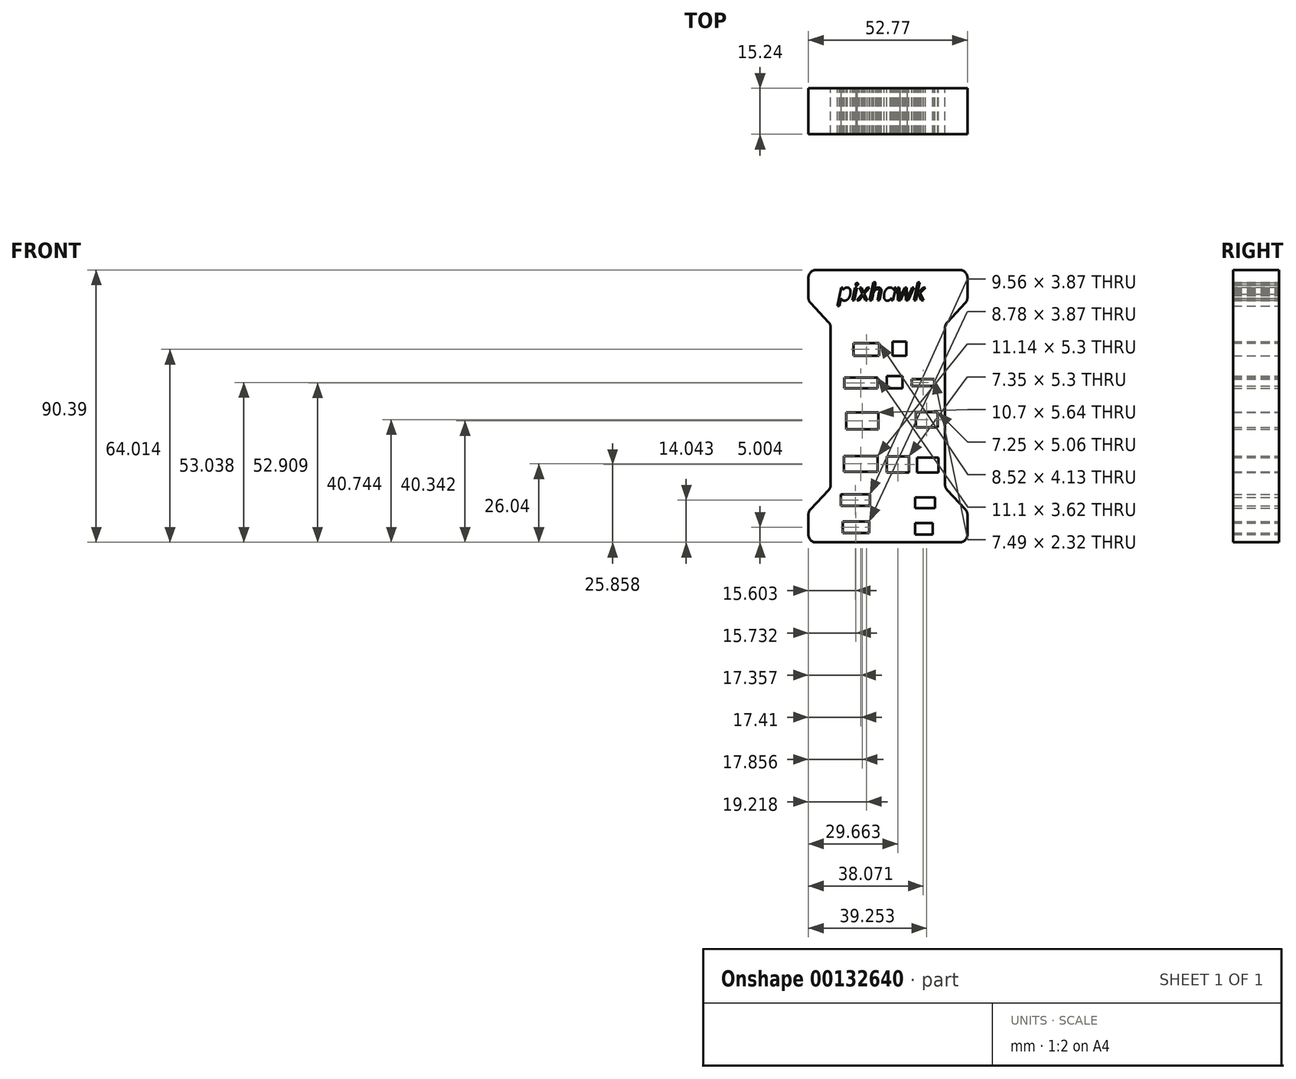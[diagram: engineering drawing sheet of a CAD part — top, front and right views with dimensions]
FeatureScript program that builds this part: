
annotation { "Feature Type Name" : "Feature", "Feature Type Description" : "" }
export const myFeature = defineFeature(function(context is Context, id is Id, definition is map)
    precondition{}
    {
        {
            var Q0;
            Q0=qCreatedBy(makeId("Front.planeOp"),FACE);
            var sketch = newSketch(context, id + "F0", { "sketchPlane" : qUnion([Q0])});
            skText(sketch, "E0", { "text": "pixhawk", "fontName": "OpenSans-Italic.ttf"});
            skLineSegment(sketch, "E1.bottom", {"start": v(-12.44, 30.78) * mm, "end": v(-3.92, 30.78) * mm});
            skLineSegment(sketch, "E1.top", {"start": v(-12.44, 26.65) * mm, "end": v(-3.92, 26.65) * mm});
            skLineSegment(sketch, "E1.left", {"start": v(-12.44, 30.78) * mm, "end": v(-12.44, 26.65) * mm});
            skLineSegment(sketch, "E1.right", {"start": v(-3.92, 30.78) * mm, "end": v(-3.92, 26.65) * mm});
            skLineSegment(sketch, "E2.bottom", {"start": v(0.47, 31.3) * mm, "end": v(5.12, 31.3) * mm});
            skLineSegment(sketch, "E2.top", {"start": v(0.47, 26.65) * mm, "end": v(5.12, 26.65) * mm});
            skLineSegment(sketch, "E2.left", {"start": v(0.47, 31.3) * mm, "end": v(0.47, 26.65) * mm});
            skLineSegment(sketch, "E2.right", {"start": v(5.12, 31.3) * mm, "end": v(5.12, 26.65) * mm});
            skLineSegment(sketch, "E3.bottom", {"start": v(-15.54, 19.42) * mm, "end": v(-4.44, 19.42) * mm});
            skLineSegment(sketch, "E3.top", {"start": v(-15.54, 15.8) * mm, "end": v(-4.44, 15.8) * mm});
            skLineSegment(sketch, "E3.left", {"start": v(-15.54, 19.42) * mm, "end": v(-15.54, 15.8) * mm});
            skLineSegment(sketch, "E3.right", {"start": v(-4.44, 19.42) * mm, "end": v(-4.44, 15.8) * mm});
            skLineSegment(sketch, "E4.bottom", {"start": v(-1.41, 19.93) * mm, "end": v(3.83, 19.93) * mm});
            skLineSegment(sketch, "E4.top", {"start": v(-1.41, 15.8) * mm, "end": v(3.83, 15.8) * mm});
            skLineSegment(sketch, "E4.left", {"start": v(-1.41, 19.93) * mm, "end": v(-1.41, 15.8) * mm});
            skLineSegment(sketch, "E4.right", {"start": v(3.83, 19.93) * mm, "end": v(3.83, 15.8) * mm});
            skLineSegment(sketch, "E5.bottom", {"start": v(6.93, 18.9) * mm, "end": v(14.42, 18.9) * mm});
            skLineSegment(sketch, "E5.top", {"start": v(6.93, 16.58) * mm, "end": v(14.42, 16.58) * mm});
            skLineSegment(sketch, "E5.left", {"start": v(6.93, 18.9) * mm, "end": v(6.93, 16.58) * mm});
            skLineSegment(sketch, "E5.right", {"start": v(14.42, 18.9) * mm, "end": v(14.42, 16.58) * mm});
            skLineSegment(sketch, "E6.bottom", {"start": v(-16.57, -19.32) * mm, "end": v(-7.02, -19.32) * mm});
            skLineSegment(sketch, "E6.top", {"start": v(-16.57, -23.2) * mm, "end": v(-7.02, -23.2) * mm});
            skLineSegment(sketch, "E6.left", {"start": v(-16.57, -19.32) * mm, "end": v(-16.57, -23.2) * mm});
            skLineSegment(sketch, "E6.right", {"start": v(-7.02, -19.32) * mm, "end": v(-7.02, -23.2) * mm});
            skLineSegment(sketch, "E7.bottom", {"start": v(-16.06, -28.36) * mm, "end": v(-7.28, -28.36) * mm});
            skLineSegment(sketch, "E7.top", {"start": v(-16.06, -32.23) * mm, "end": v(-7.28, -32.23) * mm});
            skLineSegment(sketch, "E7.left", {"start": v(-16.06, -28.36) * mm, "end": v(-16.06, -32.23) * mm});
            skLineSegment(sketch, "E7.right", {"start": v(-7.28, -28.36) * mm, "end": v(-7.28, -32.23) * mm});
            skLineSegment(sketch, "E8.bottom", {"start": v(7.96, -20.35) * mm, "end": v(14.67, -20.35) * mm});
            skLineSegment(sketch, "E8.top", {"start": v(7.96, -23.97) * mm, "end": v(14.67, -23.97) * mm});
            skLineSegment(sketch, "E8.left", {"start": v(7.96, -20.35) * mm, "end": v(7.96, -23.97) * mm});
            skLineSegment(sketch, "E8.right", {"start": v(14.67, -20.35) * mm, "end": v(14.67, -23.97) * mm});
            skLineSegment(sketch, "E9.bottom", {"start": v(7.96, -28.88) * mm, "end": v(13.9, -28.88) * mm});
            skLineSegment(sketch, "E9.top", {"start": v(7.96, -32.75) * mm, "end": v(13.9, -32.75) * mm});
            skLineSegment(sketch, "E9.left", {"start": v(7.96, -28.88) * mm, "end": v(7.96, -32.75) * mm});
            skLineSegment(sketch, "E9.right", {"start": v(13.9, -28.88) * mm, "end": v(13.9, -32.75) * mm});
            skLineSegment(sketch, "E10.bottom", {"start": v(-15.61, -6.61) * mm, "end": v(-4.47, -6.61) * mm});
            skLineSegment(sketch, "E10.top", {"start": v(-15.61, -11.9) * mm, "end": v(-4.47, -11.9) * mm});
            skLineSegment(sketch, "E10.left", {"start": v(-15.61, -6.61) * mm, "end": v(-15.61, -11.9) * mm});
            skLineSegment(sketch, "E10.right", {"start": v(-4.47, -6.61) * mm, "end": v(-4.47, -11.9) * mm});
            skLineSegment(sketch, "E11.bottom", {"start": v(-1.41, -6.8) * mm, "end": v(5.94, -6.8) * mm});
            skLineSegment(sketch, "E11.top", {"start": v(-1.41, -12.1) * mm, "end": v(5.94, -12.1) * mm});
            skLineSegment(sketch, "E11.left", {"start": v(-1.41, -6.8) * mm, "end": v(-1.41, -12.1) * mm});
            skLineSegment(sketch, "E11.right", {"start": v(5.94, -6.8) * mm, "end": v(5.94, -12.1) * mm});
            skLineSegment(sketch, "E12.bottom", {"start": v(8.68, -7.16) * mm, "end": v(15.8, -7.16) * mm});
            skLineSegment(sketch, "E12.top", {"start": v(8.68, -12.1) * mm, "end": v(15.8, -12.1) * mm});
            skLineSegment(sketch, "E12.left", {"start": v(8.68, -7.16) * mm, "end": v(8.68, -12.1) * mm});
            skLineSegment(sketch, "E12.right", {"start": v(15.8, -7.16) * mm, "end": v(15.8, -12.1) * mm});
            skLineSegment(sketch, "E13.bottom", {"start": v(-14.9, 7.86) * mm, "end": v(-4.2, 7.86) * mm});
            skLineSegment(sketch, "E13.top", {"start": v(-14.9, 2.22) * mm, "end": v(-4.2, 2.22) * mm});
            skLineSegment(sketch, "E13.left", {"start": v(-14.9, 7.86) * mm, "end": v(-14.9, 2.22) * mm});
            skLineSegment(sketch, "E13.right", {"start": v(-4.2, 7.86) * mm, "end": v(-4.2, 2.22) * mm});
            skLineSegment(sketch, "E14.bottom", {"start": v(8.23, 7.98) * mm, "end": v(15.48, 7.98) * mm});
            skLineSegment(sketch, "E14.top", {"start": v(8.23, 2.91) * mm, "end": v(15.48, 2.91) * mm});
            skLineSegment(sketch, "E14.left", {"start": v(8.23, 7.98) * mm, "end": v(8.23, 2.91) * mm});
            skLineSegment(sketch, "E14.right", {"start": v(15.48, 7.98) * mm, "end": v(15.48, 2.91) * mm});
            skLineSegment(sketch, "E15.top", {"start": v(24.97, 9.52) * mm, "end": v(-27.8, 9.52) * mm});
            skLineSegment(sketch, "E16.bottom", {"start": v(25.37, -35.3) * mm, "end": v(-27.4, -35.3) * mm});
            skLineSegment(sketch, "E16.top", {"start": v(25.37, 55.1) * mm, "end": v(-27.4, 55.1) * mm});
            skLineSegment(sketch, "E16.left", {"start": v(25.37, -35.3) * mm, "end": v(25.37, -25.07) * mm});
            skLineSegment(sketch, "E16.right", {"start": v(-27.4, -35.3) * mm, "end": v(-27.4, -25.07) * mm});
            skPoint(sketch, "E16.middle", {"position": v(-1.02, 9.9) * mm});
            skLineSegment(sketch, "E17.left", {"start": v(17.97, -17.2) * mm, "end": v(17.97, 36.99) * mm});
            skLineSegment(sketch, "E17.right", {"start": v(-20, -17.2) * mm, "end": v(-20, 36.99) * mm});
            skLineSegment(sketch, "E18", {"start": v(25.37, -25.07) * mm, "end": v(17.97, -17.2) * mm});
            skLineSegment(sketch, "E19.MirrorCS", {"start": v(-27.4, -25.07) * mm, "end": v(-20, -17.2) * mm});
            skLineSegment(sketch, "E20.MirrorCS", {"start": v(25.37, 44.87) * mm, "end": v(17.97, 36.99) * mm});
            skLineSegment(sketch, "E21.MirrorCS", {"start": v(-27.4, 44.87) * mm, "end": v(-20, 36.99) * mm});
            skLineSegment(sketch, "E22.trimOffspring", {"start": v(25.37, 44.87) * mm, "end": v(25.37, 55.1) * mm});
            skPoint(sketch, "E17.bottom.start.orphan", {"position": v(17.97, -22.79) * mm});
            skPoint(sketch, "E23.orphan", {"position": v(-20, -22.79) * mm});
            skPoint(sketch, "E17.top.start.orphan", {"position": v(17.97, 42.58) * mm});
            skPoint(sketch, "E24.orphan", {"position": v(-20, 42.58) * mm});
            skLineSegment(sketch, "E25.trimOffspring", {"start": v(-27.4, 44.87) * mm, "end": v(-27.4, 55.1) * mm});
            const initialGuessF0  = {"E0": [-0.0176, 0.04498, 1, 0, 0.00568]};
            skSetInitialGuess(sketch, initialGuessF0);
            skSolve(sketch);
        }
        {
            var Q0;
            Q0=qSketchRegion(id+"F0",true);
            extrude(context, id + "F1", {"entities" : qUnion([Q0]), "depth" : 15.24 * mm});
        }
        {
            var Q0;
            Q0=makeQuery(id+"F1.opExtrude","SWEPT_EDGE",EDGE,{"disambiguationData":[OSD([sQuery(id+"F0.wireOp",EDGE,"E21.MirrorCS"),sQuery(id+"F0.wireOp",EDGE,"E25.trimOffspring")])]});
            var Q1;
            Q1=makeQuery(id+"F1.opExtrude","SWEPT_EDGE",EDGE,{"disambiguationData":[OSD([sQuery(id+"F0.wireOp",EDGE,"E16.top"),sQuery(id+"F0.wireOp",EDGE,"E25.trimOffspring")])]});
            var Q2;
            Q2=makeQuery(id+"F1.opExtrude","SWEPT_EDGE",EDGE,{"disambiguationData":[OSD([sQuery(id+"F0.wireOp",EDGE,"E17.right"),sQuery(id+"F0.wireOp",EDGE,"E21.MirrorCS")])]});
            var Q3;
            Q3=makeQuery(id+"F1.opExtrude","SWEPT_EDGE",EDGE,{"disambiguationData":[OSD([sQuery(id+"F0.wireOp",EDGE,"E17.right"),sQuery(id+"F0.wireOp",EDGE,"E19.MirrorCS")])]});
            var Q4;
            Q4=makeQuery(id+"F1.opExtrude","SWEPT_EDGE",EDGE,{"disambiguationData":[OSD([sQuery(id+"F0.wireOp",EDGE,"E16.right"),sQuery(id+"F0.wireOp",EDGE,"E19.MirrorCS")])]});
            var Q5;
            Q5=makeQuery(id+"F1.opExtrude","SWEPT_EDGE",EDGE,{"disambiguationData":[OSD([sQuery(id+"F0.wireOp",EDGE,"E16.bottom"),sQuery(id+"F0.wireOp",EDGE,"E16.right")])]});
            var Q6;
            Q6=makeQuery(id+"F1.opExtrude","SWEPT_EDGE",EDGE,{"disambiguationData":[OSD([sQuery(id+"F0.wireOp",EDGE,"E16.bottom"),sQuery(id+"F0.wireOp",EDGE,"E16.left")])]});
            var Q7;
            Q7=makeQuery(id+"F1.opExtrude","SWEPT_EDGE",EDGE,{"disambiguationData":[OSD([sQuery(id+"F0.wireOp",EDGE,"E16.left"),sQuery(id+"F0.wireOp",EDGE,"E18")])]});
            var Q8;
            Q8=makeQuery(id+"F1.opExtrude","SWEPT_EDGE",EDGE,{"disambiguationData":[OSD([sQuery(id+"F0.wireOp",EDGE,"E17.left"),sQuery(id+"F0.wireOp",EDGE,"E18")])]});
            var Q9;
            Q9=makeQuery(id+"F1.opExtrude","SWEPT_EDGE",EDGE,{"disambiguationData":[OSD([sQuery(id+"F0.wireOp",EDGE,"E17.left"),sQuery(id+"F0.wireOp",EDGE,"E20.MirrorCS")])]});
            var Q10;
            Q10=makeQuery(id+"F1.opExtrude","SWEPT_EDGE",EDGE,{"disambiguationData":[OSD([sQuery(id+"F0.wireOp",EDGE,"E20.MirrorCS"),sQuery(id+"F0.wireOp",EDGE,"E22.trimOffspring")])]});
            var Q11;
            Q11=makeQuery(id+"F1.opExtrude","SWEPT_EDGE",EDGE,{"disambiguationData":[OSD([sQuery(id+"F0.wireOp",EDGE,"E16.top"),sQuery(id+"F0.wireOp",EDGE,"E22.trimOffspring")])]});
            fillet(context, id + "F2", {"entities" : qUnion([Q0, Q1, Q2, Q3, Q4, Q5, Q6, Q7, Q8, Q9, Q10, Q11]), "radius" : 2.54 * mm, "tangentPropagation" : true, "allowEdgeOverflow" : false});
        }
    });
